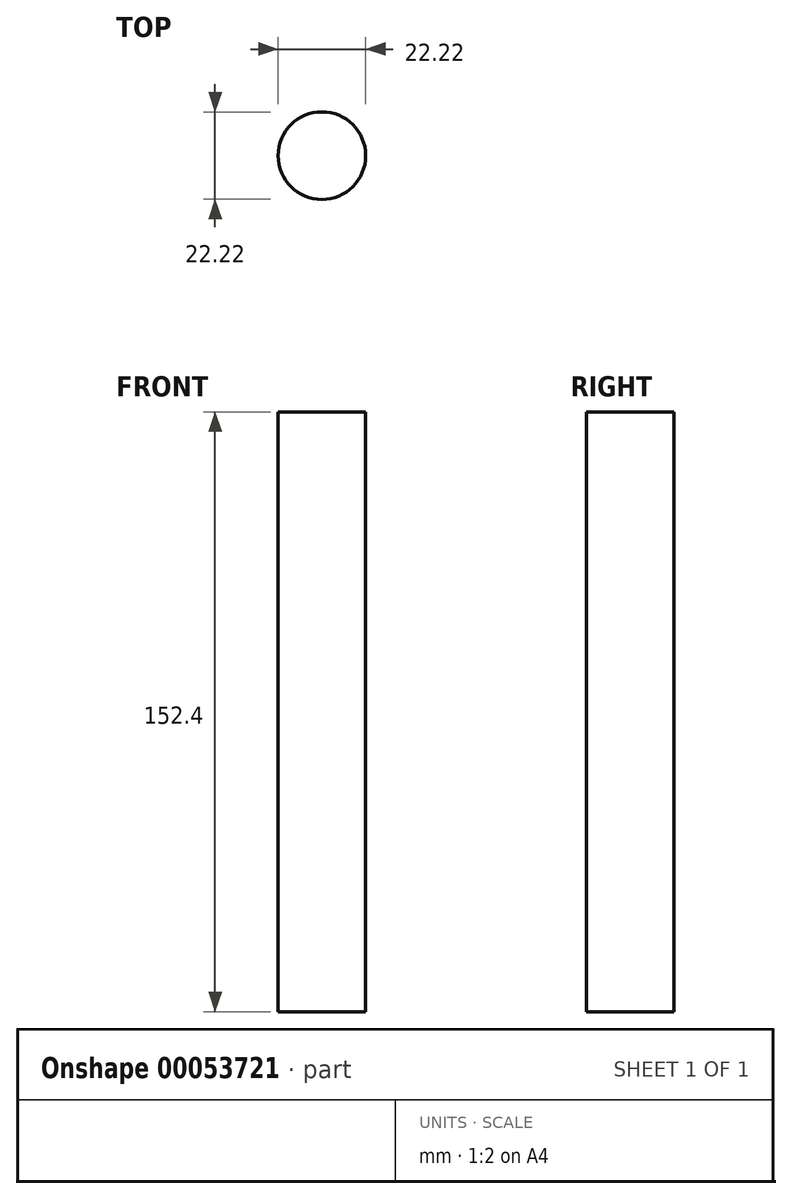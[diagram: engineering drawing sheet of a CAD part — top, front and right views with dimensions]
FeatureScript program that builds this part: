
annotation { "Feature Type Name" : "Feature", "Feature Type Description" : "" }
export const myFeature = defineFeature(function(context is Context, id is Id, definition is map)
    precondition{}
    {
        {
            var Q0;
            Q0=qCreatedBy(makeId("Top.planeOp"),FACE);
            var sketch = newSketch(context, id + "F0", { "sketchPlane" : qUnion([Q0])});
            skCircle(sketch, "E0", {"center": v(0, 0) * mm, "radius": 11.11 * mm});
            skSolve(sketch);
        }
        {
            var Q0;
            Q0 = qSketchRegion(id + "F0", true);
            extrude(context, id + "F1", {"entities" : qUnion([Q0]), "depth" : 152.4 * mm});
        }
    });
